# Revit family: 8641000
name_source: partatom
category: Aparatos sanitarios
revit_build: Autodesk Revit 2017 (Build: 20160225_1515(x64)
units: mm (PartAtom-declared; Revit-internal decimal feet)

## family parameters
Anfitrión = Cara
Compartido = No
Corte con vacíos al cargar = No
Cota de conector redondo = Diámetro de uso
Número OmniClass = 23.45.55.14
Punto de cálculo de habitación = No
Tipo de pieza = Normal
Título OmniClass = Single Faucets

## types (1)
- 8641000
    Accionamiento = Mediante maneta
    CIERRE = Manual
    Comentarios de tipo = Cartucho sellado mezclador con discos cerámicos de Ø 35 mm.  Entradas hembra de 3/4" con excéntricas y embellecedor.
    Conexión AC = Sí
    Conexión AF = Sí
    Código de montaje = C1030220
    Descripción = Grupo baño-ducha con accesorios
    ENTRADA = Hembra 3/4"
    Elevación por defecto = 1219 mm
    Fabricante = PRESTO IBÉRICA
    Imagen de tipo = <Ninguno>
    Material = LATON CROMADO
    Modelo = GRUPO BAÑO-DUCHA con accesorios
    PESO BRUTO = 4.52 Kg
    Presión Máxima = 8 bar
    REFERENCIA = 8641000
    TIPO DE AGUA = Fria/Caliente
    Teléfono = (+34) 915 782 575
    URL = http://www.griferiasgalindo.com
